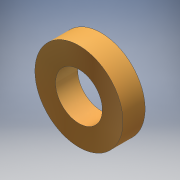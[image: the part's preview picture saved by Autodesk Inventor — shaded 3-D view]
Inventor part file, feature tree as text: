
AUTODESK INVENTOR PART (.ipt)
format: ipt  version: 2016 (Build 200138000, 138)  size: 119,296 bytes
history: native  units: mm
features: extrude x1, sketch x1
ambient origin geometry x8: Origin, YZ Plane, XZ Plane, XY Plane, X Axis, Y Axis, Z Axis, Center Point
bodies: Solid1 (feature_tree)
feature tree (2):
  extrude  "Extrusion1"  Depth=3.0mm
  sketch  "Sketch1"  dims[d0=6.35mm d1=11.9375mm d2=3.0mm d3=0.0mm]
